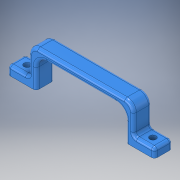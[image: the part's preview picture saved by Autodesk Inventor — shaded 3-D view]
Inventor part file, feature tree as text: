
AUTODESK INVENTOR PART (.ipt)
format: ipt  version: 2019.2 (Build 232265000, 265)  size: 224,768 bytes
history: native  units: in
note: dims shown in document units (in); Inventor stores cm internally (conversion verified against a paired STEP export)
features: fillet x5, sketch x2, extrude x1, hole x1
ambient origin geometry x8: Origin, YZ Plane, XZ Plane, XY Plane, X Axis, Y Axis, Z Axis, Center Point
bodies: Solid1 (feature_tree)
feature tree (9):
  extrude  "Extrusion1"  Depth=0.3125in
  hole  "Hole1"  [1 undecoded]
  fillet  "Fillet1"  Radius=1.875in
  fillet  "Fillet2"  Radius=0.75in
  fillet  "Fillet3"  [1 undecoded]
  fillet  "Fillet4"  Radius=0.375in
  fillet  "Fillet5"  Radius=0.4375in
  sketch  "Sketch1"  dims[d7=0.3125in d8=0.3125in]
  sketch  "Sketch2"  dims[d10=0.375in d11=1.25in d12=1.875in d13=0.75in d14=0.0in d15=0.266in d16=0.75in d17=0.507in d18=0.25in d19=0.5635in d20=1.0in d21=0.8108in d22=0.375in d23=0.4375in d24=0.125in d25=0.125in d26=0.125in d27=0.875in d28=1.5625in]
note: 2 required parameter values undecoded (feature->parameter linkage not recoverable at this tier; creation-order binding heuristic only, values carry confidence <= 0.55)
